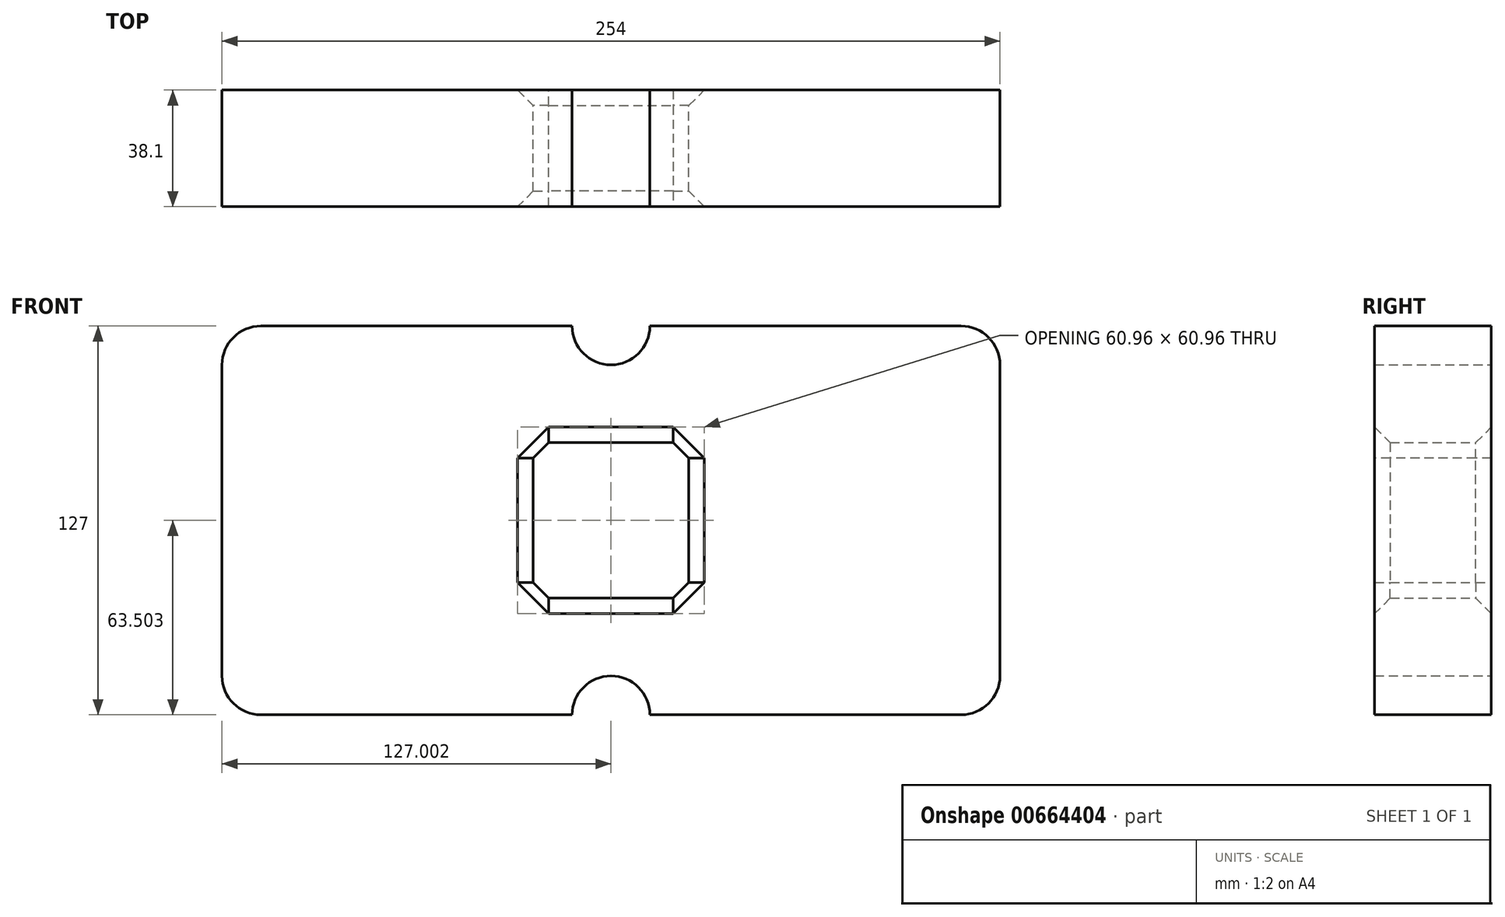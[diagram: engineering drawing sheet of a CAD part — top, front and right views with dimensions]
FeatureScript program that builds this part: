
annotation { "Feature Type Name" : "Feature", "Feature Type Description" : "" }
export const myFeature = defineFeature(function(context is Context, id is Id, definition is map)
    precondition{}
    {
        {
            var Q0;
            Q0=qCreatedBy(makeId("Front.planeOp"),FACE);
            var sketch = newSketch(context, id + "F0", { "sketchPlane" : qUnion([Q0])});
            skLineSegment(sketch, "E0.bottom", {"start": v(-114, 69.22) * mm, "end": v(-12.4, 69.22) * mm});
            skLineSegment(sketch, "E0.top", {"start": v(-114, -57.78) * mm, "end": v(-12.4, -57.78) * mm});
            skLineSegment(sketch, "E0.left", {"start": v(-126.7, 56.52) * mm, "end": v(-126.7, -45.08) * mm});
            skLineSegment(sketch, "E0.right", {"start": v(127.3, 56.52) * mm, "end": v(127.3, -45.08) * mm});
            skPoint(sketch, "E1.visualSharp", {"position": v(-126.7, 69.22) * mm});
            skArc(sketch, "E1.filletArc", {"start": v(-114, 69.22) * mm, "mid": v(-122.98, 65.5) * mm, "end": v(-126.7, 56.52) * mm});
            skPoint(sketch, "E2.visualSharp", {"position": v(-126.7, -57.78) * mm});
            skArc(sketch, "E2.filletArc", {"start": v(-126.7, -45.08) * mm, "mid": v(-122.98, -54.06) * mm, "end": v(-114, -57.78) * mm});
            skPoint(sketch, "E3.visualSharp", {"position": v(127.3, 69.22) * mm});
            skArc(sketch, "E3.filletArc", {"start": v(127.3, 56.52) * mm, "mid": v(123.58, 65.5) * mm, "end": v(114.6, 69.22) * mm});
            skPoint(sketch, "E4.visualSharp", {"position": v(127.3, -57.78) * mm});
            skArc(sketch, "E4.filletArc", {"start": v(114.6, -57.78) * mm, "mid": v(123.58, -54.06) * mm, "end": v(127.3, -45.08) * mm});
            skArc(sketch, "E5", {"start": v(13, -57.78) * mm, "mid": v(0.3, -45.08) * mm, "end": v(-12.4, -57.78) * mm});
            skArc(sketch, "E6", {"start": v(-12.4, 69.22) * mm, "mid": v(0.3, 56.52) * mm, "end": v(13, 69.22) * mm});
            skLineSegment(sketch, "E7.trimOffspring", {"start": v(13, -57.78) * mm, "end": v(114.6, -57.78) * mm});
            skLineSegment(sketch, "E8.trimOffspring", {"start": v(13, 69.22) * mm, "end": v(114.6, 69.22) * mm});
            skLineSegment(sketch, "E9", {"start": v(-25.1, 31.12) * mm, "end": v(-25.1, -19.68) * mm});
            skLineSegment(sketch, "E10", {"start": v(-25.1, -19.68) * mm, "end": v(25.7, -19.68) * mm});
            skLineSegment(sketch, "E11", {"start": v(25.7, -19.68) * mm, "end": v(25.7, 31.12) * mm});
            skPoint(sketch, "E12.end.orphan", {"position": v(-34.16, 31.12) * mm});
            skLineSegment(sketch, "E13", {"start": v(-25.1, 31.12) * mm, "end": v(25.7, 31.12) * mm});
            skSolve(sketch);
        }
        {
            var Q0;
            Q0 = qSketchRegion(id + "F0", true);
            extrude(context, id + "F1", {"entities" : qUnion([Q0]), "depth" : 38.1 * mm, "offsetDistance" : 25.4 * mm});
        }
        {
            var Q0;
            Q0=makeQuery(id+"F1.opExtrude","SWEPT_FACE",FACE,{"disambiguationData":[OSD([sQuery(id+"F0.wireOp",EDGE,"E11")])]});
            var Q1;
            Q1=makeQuery(id+"F1.opExtrude","SWEPT_FACE",FACE,{"disambiguationData":[OSD([sQuery(id+"F0.wireOp",EDGE,"E13")])]});
            var Q2;
            Q2=makeQuery(id+"F1.opExtrude","SWEPT_FACE",FACE,{"disambiguationData":[OSD([sQuery(id+"F0.wireOp",EDGE,"E10")])]});
            var Q3;
            Q3=makeQuery(id+"F1.opExtrude","SWEPT_FACE",FACE,{"disambiguationData":[OSD([sQuery(id+"F0.wireOp",EDGE,"E9")])]});
            chamfer(context, id + "F2", {"entities" : qUnion([Q0, Q1, Q2, Q3]), "width" : 5.08 * mm, "tangentPropagation" : true});
        }
    });
